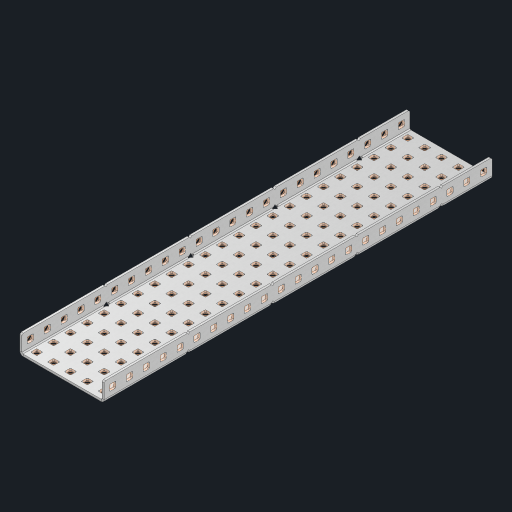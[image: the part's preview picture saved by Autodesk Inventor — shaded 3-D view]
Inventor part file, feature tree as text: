
AUTODESK INVENTOR PART (.ipt)
format: ipt  version: 2023 (Build 270158000, 158)  size: 1,828,864 bytes
history: native  units: in
note: dims shown in document units (in); Inventor stores cm internally (conversion verified against a paired STEP export)
features: other x166, extrude x160, sheet_metal_op x10, sketch x8, mirror x1, pattern_linear x1, chamfer x1
ambient origin geometry x8: Origin, YZ Plane, XZ Plane, XY Plane, X Axis, Y Axis, Z Axis, Center Point
bodies: Solid1 (feature_tree), Body (feature_tree)
feature tree (347):
  other  "Flange Pattern Plane"
  sheet_metal_op  "Flange Pattern"
  sheet_metal_op  "Body Pattern"
  other  "Arc Length"
  mirror  "Notch Mirror"
  pattern_linear  "Notch Pattern"  Spacing1=0.25in  [1 undecoded]
  chamfer  "End Chamfer"
  extrude  "Half Cut"  Depth=0.0625in
  sketch  "Sketch1"  dims[d0=2.5in]
  other  "Plate1"
  sketch  "Sketch2"  dims[d1=11.5in]
  other  "Plate2"
  sheet_metal_op  "Bend1"
  sheet_metal_op  "Corner1"
  sketch  "Sketch3"  dims[d2=0.0625in]
  other  "Flange Pattern Sketch"
  sketch  "Sketch7"  dims[d3=0.0625in]
  other  "Srf1"
  other  "Srf2"
  sketch  "Sketch8"  dims[d4=0.0312in]
  sketch  "Sketch9"  dims[d5=0.125in]
  other  "Srf91"
  sheet_metal_op  "Body Pattern Sketch"
  other  "Srf92"
  sketch  "Sketch13"  dims[d6=0.0625in]
  sketch  "Sketch14"  dims[d7=0.5in d8=90.0deg d9=0.0312in d10=0.25in d11=0.0625in d12=0.0625in d16=0.182in d17=0.02in d18=0.0625in d19=0.0in d20=0.25in d21=0.25in d46=0.172in d47=1.0in d48=0.0in d49=0.182in d50=0.02in d51=0.25in d52=0.25in d53=0.0625in d54=0.0in d55=0.172in d56=1.0in d57=0.0in d60=9.0551in d62=0.5in d63=1.9685in d65=0.5in d85=0.1473in d86=0.1782in d88=0.04in d89=0.0625in d90=0.0in d91=0.04in d92=0.0491in d95=2.5in d96=0.04in d97=0.25in d98=45.0deg d101=0.0in d102=2.497in d131=2.5in d132=9.0551in d134=0.5in d139=0.5in]
  other  "Srf856"
  other  "Srf1310"
  other  "Srf1311"
  other  "Srf1312"
  other  "Srf1376"
  other  "Srf1377"
  other  "Srf1728"
  other  "Srf1755"
  other  "Srf1878"
  other  "Srf1879"
  other  "Srf1880"
  other  "Srf1881"
  other  "Srf1882"
  other  "Srf1883"
  other  "Srf1884"
  other  "Srf1885"
  other  "Srf1886"
  other  "Srf1887"
  other  "Srf1888"
  other  "Srf1889"
  other  "Srf1890"
  other  "Srf1891"
  other  "Srf1892"
  other  "Srf1893"
  other  "Srf1894"
  other  "Srf1895"
  other  "Srf1896"
  other  "Srf1897"
  other  "Srf1898"
  other  "Srf1899"
  other  "Srf1900"
  other  "Srf1901"
  other  "Srf1902"
  other  "Srf1903"
  other  "Srf1904"
  other  "Srf1905"
  other  "Srf1906"
  other  "Srf1942"
  other  "Srf1943"
  other  "Srf1944"
  other  "Srf1945"
  other  "Srf1946"
  other  "Srf1947"
  other  "Srf1948"
  other  "Srf1949"
  other  "Srf1950"
  other  "Srf1951"
  other  "Srf1952"
  other  "Srf1953"
  other  "Srf1954"
  other  "Srf1955"
  other  "Srf1956"
  other  "Srf1957"
  other  "Srf1958"
  other  "Srf1959"
  other  "Srf1960"
  other  "Srf1961"
  other  "Srf1962"
  other  "Srf1963"
  other  "Srf1964"
  other  "Srf1965"
  other  "Srf1966"
  other  "Srf1967"
  other  "Srf1968"
  other  "Srf1969"
  other  "Srf1970"
  other  "Srf2111"
  other  "Srf2112"
  other  "Srf2113"
  other  "Srf2114"
  other  "Srf2115"
  other  "Srf2116"
  other  "Srf2117"
  other  "Srf2118"
  other  "Srf2119"
  other  "Srf2120"
  other  "Srf2121"
  other  "Srf2146"
  other  "Srf2147"
  other  "Srf2148"
  other  "Srf2149"
  other  "Srf2150"
  other  "Srf2151"
  other  "Srf2152"
  other  "Srf2153"
  other  "Srf2154"
  other  "Srf2155"
  other  "Srf2156"
  other  "Srf2157"
  other  "Srf2158"
  other  "Srf2159"
  other  "Srf2160"
  other  "Srf2161"
  other  "Srf2162"
  other  "Srf2163"
  other  "Srf2164"
  other  "Srf2165"
  other  "Srf2166"
  other  "Srf2167"
  other  "Srf2168"
  other  "Srf2169"
  other  "Srf2170"
  other  "Srf2171"
  other  "Srf2172"
  other  "Srf2173"
  other  "Srf2174"
  other  "Srf2175"
  other  "Srf2176"
  other  "Srf2177"
  other  "Srf2178"
  other  "Srf2179"
  other  "Srf2180"
  other  "Srf2181"
  other  "Srf2182"
  other  "Srf2183"
  other  "Srf2184"
  other  "Srf2185"
  other  "Srf2186"
  other  "Srf2187"
  other  "Srf2188"
  other  "Srf2189"
  other  "Srf2190"
  other  "Srf2191"
  other  "Srf2192"
  other  "Srf2193"
  other  "Srf2194"
  other  "Srf2195"
  other  "Srf2196"
  other  "Srf2197"
  other  "Srf2198"
  other  "Srf2199"
  other  "Srf2200"
  other  "Srf2201"
  other  "Srf2202"
  other  "Srf2203"
  other  "Srf2204"
  other  "Srf2205"
  other  "Srf2206"
  other  "Srf2207"
  other  "Srf2208"
  other  "Srf2209"
  other  "Srf2210"
  other  "Srf2211"
  other  "Srf2212"
  other  "Srf2213"
  other  "Srf2214"
  other  "Srf2215"
  other  "Srf2216"
  other  "Srf2217"
  other  "Srf2218"
  other  "Srf2219"
  other  "Srf2220"
  other  "Srf2221"
  other  "Srf2222"
  other  "Srf2223"
  other  "Srf2224"
  other  "Srf2225"
  sheet_metal_op  "Flange Stamp"
  sheet_metal_op  "Flange Circle"
  sheet_metal_op  "Body Stamp"
  sheet_metal_op  "Body Circle"
  sheet_metal_op  "Notch"
  extrude  "ExtrusionSrf2"  Depth=0.0625in
  extrude  "ExtrusionSrf92"  Depth=2.5in
  extrude  "ExtrusionSrf856"  Depth=0.02in
  extrude  "ExtrusionSrf1310"  Depth=0.0625in
  extrude  "ExtrusionSrf1311"  TaperAngle=0.0deg  [1 undecoded]
  extrude  "ExtrusionSrf1312"  Depth=0.25in
  extrude  "ExtrusionSrf1376"  Depth=0.25in
  extrude  "ExtrusionSrf1377"  Depth=2.5in
  extrude  "ExtrusionSrf1728"  Depth=2.5in TaperAngle=0.0deg
  extrude  "ExtrusionSrf1755"  Depth=2.5in
  extrude  "ExtrusionSrf1878"  Depth=0.02in
  extrude  "ExtrusionSrf1879"  Depth=0.25in
  extrude  "ExtrusionSrf1880"  Depth=0.25in
  extrude  "ExtrusionSrf1881"  Depth=0.0625in
  extrude  "ExtrusionSrf1882"  TaperAngle=0.0deg  [1 undecoded]
  extrude  "ExtrusionSrf1883"  Depth=2.5in
  extrude  "ExtrusionSrf1884"  Depth=2.5in TaperAngle=0.0deg
  extrude  "ExtrusionSrf1885"  Depth=2.5in
  extrude  "ExtrusionSrf1886"  Depth=2.5in
  extrude  "ExtrusionSrf1887"  Depth=2.5in
  extrude  "ExtrusionSrf1888"  Depth=2.5in
  extrude  "ExtrusionSrf1889"  Depth=2.5in
  extrude  "ExtrusionSrf1890"  Depth=0.0625in
  extrude  "ExtrusionSrf1891"  TaperAngle=0.0deg  [1 undecoded]
  extrude  "ExtrusionSrf1892"  Depth=2.5in
  extrude  "ExtrusionSrf1893"  Depth=2.5in
  extrude  "ExtrusionSrf1894"  Depth=2.5in
  extrude  "ExtrusionSrf1895"  Depth=0.25in TaperAngle=45.0deg
  extrude  "ExtrusionSrf1896"  TaperAngle=0.0deg  [1 undecoded]
  extrude  "ExtrusionSrf1897"  Depth=2.5in
  extrude  "ExtrusionSrf1898"  Depth=2.5in
  extrude  "ExtrusionSrf1899"  Depth=2.5in
  extrude  "ExtrusionSrf1900"  Depth=2.5in
  extrude  "ExtrusionSrf1901"  Depth=2.5in
  extrude  "ExtrusionSrf1902"  [1 undecoded]
  extrude  "ExtrusionSrf1903"  [1 undecoded]
  extrude  "ExtrusionSrf1904"  [1 undecoded]
  extrude  "ExtrusionSrf1905"  [1 undecoded]
  extrude  "ExtrusionSrf1906"  [1 undecoded]
  extrude  "ExtrusionSrf1942"  [1 undecoded]
  extrude  "ExtrusionSrf1943"  [1 undecoded]
  extrude  "ExtrusionSrf1944"  [1 undecoded]
  extrude  "ExtrusionSrf1945"  [1 undecoded]
  extrude  "ExtrusionSrf1946"  [1 undecoded]
  extrude  "ExtrusionSrf1947"  [1 undecoded]
  extrude  "ExtrusionSrf1948"  [1 undecoded]
  extrude  "ExtrusionSrf1949"  [1 undecoded]
  extrude  "ExtrusionSrf1950"  [1 undecoded]
  extrude  "ExtrusionSrf1951"  [1 undecoded]
  extrude  "ExtrusionSrf1952"  [1 undecoded]
  extrude  "ExtrusionSrf1953"  [1 undecoded]
  extrude  "ExtrusionSrf1954"  [1 undecoded]
  extrude  "ExtrusionSrf1955"  [1 undecoded]
  extrude  "ExtrusionSrf1956"  [1 undecoded]
  extrude  "ExtrusionSrf1957"  [1 undecoded]
  extrude  "ExtrusionSrf1958"  [1 undecoded]
  extrude  "ExtrusionSrf1959"  [1 undecoded]
  extrude  "ExtrusionSrf1960"  [1 undecoded]
  extrude  "ExtrusionSrf1961"  [1 undecoded]
  extrude  "ExtrusionSrf1962"  [1 undecoded]
  extrude  "ExtrusionSrf1963"  [1 undecoded]
  extrude  "ExtrusionSrf1964"  [1 undecoded]
  extrude  "ExtrusionSrf1965"  [1 undecoded]
  extrude  "ExtrusionSrf1966"  [1 undecoded]
  extrude  "ExtrusionSrf1967"  [1 undecoded]
  extrude  "ExtrusionSrf1968"  [1 undecoded]
  extrude  "ExtrusionSrf1969"  [1 undecoded]
  extrude  "ExtrusionSrf1970"  [1 undecoded]
  extrude  "ExtrusionSrf2111"  [1 undecoded]
  extrude  "ExtrusionSrf2112"  [1 undecoded]
  extrude  "ExtrusionSrf2113"  [1 undecoded]
  extrude  "ExtrusionSrf2114"  [1 undecoded]
  extrude  "ExtrusionSrf2115"  [1 undecoded]
  extrude  "ExtrusionSrf2116"  [1 undecoded]
  extrude  "ExtrusionSrf2117"  [1 undecoded]
  extrude  "ExtrusionSrf2118"  [1 undecoded]
  extrude  "ExtrusionSrf2119"  [1 undecoded]
  extrude  "ExtrusionSrf2120"  [1 undecoded]
  extrude  "ExtrusionSrf2121"  [1 undecoded]
  extrude  "ExtrusionSrf2146"  [1 undecoded]
  extrude  "ExtrusionSrf2147"  [1 undecoded]
  extrude  "ExtrusionSrf2148"  [1 undecoded]
  extrude  "ExtrusionSrf2149"  [1 undecoded]
  extrude  "ExtrusionSrf2150"  [1 undecoded]
  extrude  "ExtrusionSrf2151"  [1 undecoded]
  extrude  "ExtrusionSrf2152"  [1 undecoded]
  extrude  "ExtrusionSrf2153"  [1 undecoded]
  extrude  "ExtrusionSrf2154"  [1 undecoded]
  extrude  "ExtrusionSrf2155"  [1 undecoded]
  extrude  "ExtrusionSrf2156"  [1 undecoded]
  extrude  "ExtrusionSrf2157"  [1 undecoded]
  extrude  "ExtrusionSrf2158"  [1 undecoded]
  extrude  "ExtrusionSrf2159"  [1 undecoded]
  extrude  "ExtrusionSrf2160"  [1 undecoded]
  extrude  "ExtrusionSrf2161"  [1 undecoded]
  extrude  "ExtrusionSrf2162"  [1 undecoded]
  extrude  "ExtrusionSrf2163"  [1 undecoded]
  extrude  "ExtrusionSrf2164"  [1 undecoded]
  extrude  "ExtrusionSrf2165"  [1 undecoded]
  extrude  "ExtrusionSrf2166"  [1 undecoded]
  extrude  "ExtrusionSrf2167"  [1 undecoded]
  extrude  "ExtrusionSrf2168"  [1 undecoded]
  extrude  "ExtrusionSrf2169"  [1 undecoded]
  extrude  "ExtrusionSrf2170"  [1 undecoded]
  extrude  "ExtrusionSrf2171"  [1 undecoded]
  extrude  "ExtrusionSrf2172"  [1 undecoded]
  extrude  "ExtrusionSrf2173"  [1 undecoded]
  extrude  "ExtrusionSrf2174"  [1 undecoded]
  extrude  "ExtrusionSrf2175"  [1 undecoded]
  extrude  "ExtrusionSrf2176"  [1 undecoded]
  extrude  "ExtrusionSrf2177"  [1 undecoded]
  extrude  "ExtrusionSrf2178"  [1 undecoded]
  extrude  "ExtrusionSrf2179"  [1 undecoded]
  extrude  "ExtrusionSrf2180"  [1 undecoded]
  extrude  "ExtrusionSrf2181"  [1 undecoded]
  extrude  "ExtrusionSrf2182"  [1 undecoded]
  extrude  "ExtrusionSrf2183"  [1 undecoded]
  extrude  "ExtrusionSrf2184"  [1 undecoded]
  extrude  "ExtrusionSrf2185"  [1 undecoded]
  extrude  "ExtrusionSrf2186"  [1 undecoded]
  extrude  "ExtrusionSrf2187"  [1 undecoded]
  extrude  "ExtrusionSrf2188"  [1 undecoded]
  extrude  "ExtrusionSrf2189"  [1 undecoded]
  extrude  "ExtrusionSrf2190"  [1 undecoded]
  extrude  "ExtrusionSrf2191"  [1 undecoded]
  extrude  "ExtrusionSrf2192"  [1 undecoded]
  extrude  "ExtrusionSrf2193"  [1 undecoded]
  extrude  "ExtrusionSrf2194"  [1 undecoded]
  extrude  "ExtrusionSrf2195"  [1 undecoded]
  extrude  "ExtrusionSrf2196"  [1 undecoded]
  extrude  "ExtrusionSrf2197"  [1 undecoded]
  extrude  "ExtrusionSrf2198"  [1 undecoded]
  extrude  "ExtrusionSrf2199"  [1 undecoded]
  extrude  "ExtrusionSrf2200"  [1 undecoded]
  extrude  "ExtrusionSrf2201"  [1 undecoded]
  extrude  "ExtrusionSrf2202"  [1 undecoded]
  extrude  "ExtrusionSrf2203"  [1 undecoded]
  extrude  "ExtrusionSrf2204"  [1 undecoded]
  extrude  "ExtrusionSrf2205"  [1 undecoded]
  extrude  "ExtrusionSrf2206"  [1 undecoded]
  extrude  "ExtrusionSrf2207"  [1 undecoded]
  extrude  "ExtrusionSrf2208"  [1 undecoded]
  extrude  "ExtrusionSrf2209"  [1 undecoded]
  extrude  "ExtrusionSrf2210"  [1 undecoded]
  extrude  "ExtrusionSrf2211"  [1 undecoded]
  extrude  "ExtrusionSrf2212"  [1 undecoded]
  extrude  "ExtrusionSrf2213"  [1 undecoded]
  extrude  "ExtrusionSrf2214"  [1 undecoded]
  extrude  "ExtrusionSrf2215"  [1 undecoded]
  extrude  "ExtrusionSrf2216"  [1 undecoded]
  extrude  "ExtrusionSrf2217"  [1 undecoded]
  extrude  "ExtrusionSrf2218"  [1 undecoded]
  extrude  "ExtrusionSrf2219"  [1 undecoded]
  extrude  "ExtrusionSrf2220"  [1 undecoded]
  extrude  "ExtrusionSrf2221"  [1 undecoded]
  extrude  "ExtrusionSrf2222"  [1 undecoded]
  extrude  "ExtrusionSrf2223"  [1 undecoded]
  extrude  "ExtrusionSrf2224"  [1 undecoded]
  extrude  "ExtrusionSrf2225"  [1 undecoded]
note: 130 required parameter values undecoded (feature->parameter linkage not recoverable at this tier; creation-order binding heuristic only, values carry confidence <= 0.55)
